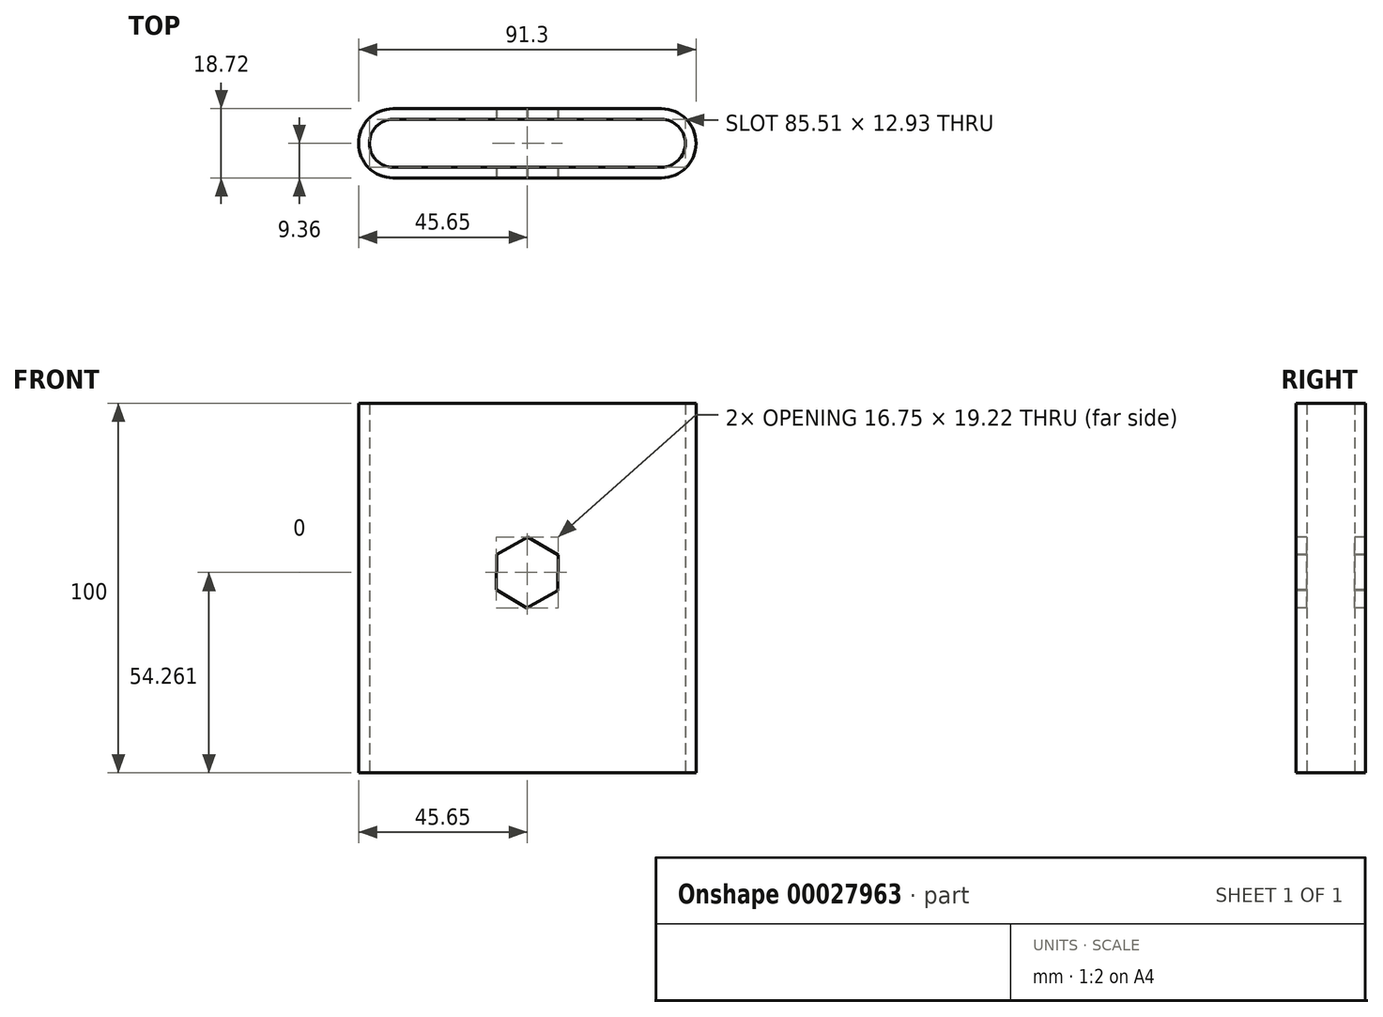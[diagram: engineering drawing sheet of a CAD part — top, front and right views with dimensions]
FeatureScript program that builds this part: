
annotation { "Feature Type Name" : "Feature", "Feature Type Description" : "" }
export const myFeature = defineFeature(function(context is Context, id is Id, definition is map)
    precondition{}
    {
        {
            var Q0;
            Q0=qCreatedBy(makeId("Top.planeOp"),FACE);
            var sketch = newSketch(context, id + "F0", { "sketchPlane" : qUnion([Q0])});
            skLineSegment(sketch, "E0.rect.bottom", {"start": v(36.29, 9.36) * mm, "end": v(-36.29, 9.36) * mm});
            skLineSegment(sketch, "E0.rect.top", {"start": v(36.29, -9.36) * mm, "end": v(-36.29, -9.36) * mm});
            skLineSegment(sketch, "E0.rect.left", {"start": v(36.29, 9.36) * mm, "end": v(36.29, -9.36) * mm});
            skLineSegment(sketch, "E0.rect.right", {"start": v(-36.29, 9.36) * mm, "end": v(-36.29, -9.36) * mm});
            skPoint(sketch, "E0.rect.middle", {"position": v(0, 0) * mm});
            skArc(sketch, "E1", {"start": v(-36.29, 9.36) * mm, "mid": v(-45.65, 0) * mm, "end": v(-36.29, -9.36) * mm});
            skArc(sketch, "E2", {"start": v(36.29, -9.36) * mm, "mid": v(45.65, 0) * mm, "end": v(36.29, 9.36) * mm});
            skLineSegment(sketch, "E3.rect.bottom", {"start": v(36.29, 6.47) * mm, "end": v(-36.29, 6.47) * mm});
            skLineSegment(sketch, "E3.rect.top", {"start": v(36.29, -6.47) * mm, "end": v(-36.29, -6.47) * mm});
            skLineSegment(sketch, "E3.rect.left", {"start": v(36.29, 6.47) * mm, "end": v(36.29, -6.47) * mm});
            skLineSegment(sketch, "E3.rect.right", {"start": v(-36.29, 6.47) * mm, "end": v(-36.29, -6.47) * mm});
            skArc(sketch, "E4", {"start": v(-36.29, 6.47) * mm, "mid": v(-42.76, 0) * mm, "end": v(-36.29, -6.47) * mm});
            skArc(sketch, "E5", {"start": v(36.29, -6.47) * mm, "mid": v(42.76, 0) * mm, "end": v(36.29, 6.47) * mm});
            skSolve(sketch);
        }
        {
            var Q0;
            Q0 = qSketchRegion(id + "F0", true);
            extrude(context, id + "F1", {"entities" : qUnion([Q0]), "depth" : 100 * mm});
        }
        {
            var Q0;
            Q0=makeQuery(id+"F1.opExtrude","SWEPT_FACE",FACE,{"disambiguationData":[OSD([sQuery(id+"F0.wireOp",EDGE,"E0.rect.top")])]});
            var sketch = newSketch(context, id + "F2", { "sketchPlane" : qUnion([Q0])});
            skCircle(sketch, "E6.cCircle", {"center": v(0, 54.26) * mm, "radius": 8.32 * mm, "construction": true});
            skLineSegment(sketch, "E6.0", {"start": v(0.1, 63.87) * mm, "end": v(8.38, 58.97) * mm});
            skLineSegment(sketch, "E6.1", {"start": v(8.38, 58.97) * mm, "end": v(8.27, 49.36) * mm});
            skLineSegment(sketch, "E6.2", {"start": v(8.27, 49.36) * mm, "end": v(-0.1, 44.65) * mm});
            skLineSegment(sketch, "E6.3", {"start": v(-0.1, 44.65) * mm, "end": v(-8.38, 49.55) * mm});
            skLineSegment(sketch, "E6.4", {"start": v(-8.38, 49.55) * mm, "end": v(-8.27, 59.16) * mm});
            skLineSegment(sketch, "E6.5", {"start": v(-8.27, 59.16) * mm, "end": v(0.1, 63.87) * mm});
            skPoint(sketch, "E6.0.midPoint", {"position": v(4.24, 61.42) * mm});
            skSolve(sketch);
        }
        {
            var Q0;
            Q0 = qSketchRegion(id + "F2", true);
            extrude(context, id + "F3", {"entities" : qUnion([Q0]), "operationType" : NewBodyOperationType.REMOVE, "endBound" : BoundingType.THROUGH_ALL, "oppositeDirection" : true, "depth" : 25 * mm});
        }
    });
